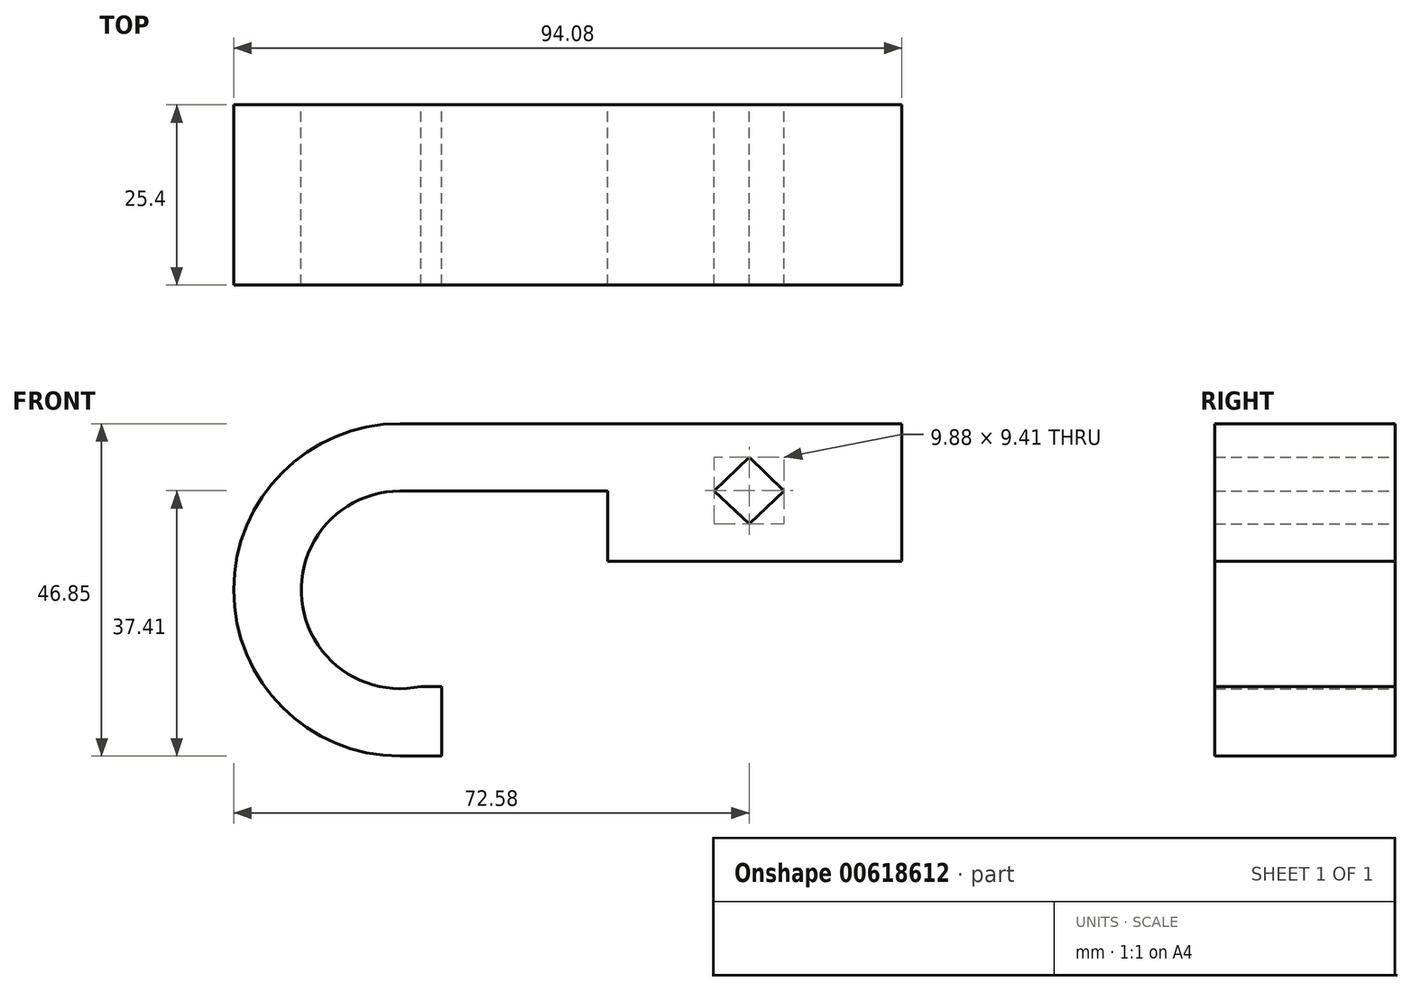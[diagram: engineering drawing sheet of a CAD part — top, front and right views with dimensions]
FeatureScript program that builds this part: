
annotation { "Feature Type Name" : "Feature", "Feature Type Description" : "" }
export const myFeature = defineFeature(function(context is Context, id is Id, definition is map)
    precondition{}
    {
        {
            var Q0;
            Q0=qCreatedBy(makeId("Front.planeOp"),FACE);
            var sketch = newSketch(context, id + "F0", { "sketchPlane" : qUnion([Q0])});
            skLineSegment(sketch, "E0.bottom", {"start": v(0, 0) * mm, "end": v(-70.66, 0) * mm});
            skLineSegment(sketch, "E0.left", {"start": v(0, 0) * mm, "end": v(0, -9.5) * mm});
            skPoint(sketch, "E1", {"position": v(-70.66, -23.42) * mm});
            skArc(sketch, "E2", {"start": v(-70.66, 0) * mm, "mid": v(-94.08, -23.42) * mm, "end": v(-70.66, -46.85) * mm});
            skArc(sketch, "E3", {"start": v(-70.66, -9.5) * mm, "mid": v(-84.5, -24.89) * mm, "end": v(-67.74, -37.03) * mm});
            skLineSegment(sketch, "E4", {"start": v(-67.74, -37.03) * mm, "end": v(-64.78, -37.03) * mm});
            skLineSegment(sketch, "E5", {"start": v(-64.78, -46.85) * mm, "end": v(-70.66, -46.85) * mm});
            skLineSegment(sketch, "E6", {"start": v(-64.78, -37.03) * mm, "end": v(-64.78, -46.85) * mm});
            skLineSegment(sketch, "E7.top", {"start": v(-41.44, -19.4) * mm, "end": v(0, -19.4) * mm});
            skLineSegment(sketch, "E7.left", {"start": v(-41.44, -9.5) * mm, "end": v(-41.44, -19.4) * mm});
            skLineSegment(sketch, "E7.right", {"start": v(0, -9.5) * mm, "end": v(0, -19.4) * mm});
            skLineSegment(sketch, "E8", {"start": v(-21.5, -4.73) * mm, "end": v(-16.56, -9.5) * mm});
            skLineSegment(sketch, "E9", {"start": v(-26.44, -9.5) * mm, "end": v(-21.5, -4.73) * mm});
            skLineSegment(sketch, "E10", {"start": v(-26.44, -9.5) * mm, "end": v(-21.5, -14.15) * mm});
            skLineSegment(sketch, "E11", {"start": v(-21.5, -14.15) * mm, "end": v(-16.56, -9.5) * mm});
            skLineSegment(sketch, "E12.trimOffspring", {"start": v(-41.44, -9.5) * mm, "end": v(-70.66, -9.5) * mm});
            skSolve(sketch);
        }
        {
            var Q0;
            Q0=makeQuery(id+"F0.imprint","IMPRINT",FACE,{"disambiguationData":[TD([[makeQuery(id+"F0.imprint","IMPRINT",EDGE,{"derivedFrom":sQuery(id+"F0.wireOp",EDGE,"E0.bottom")}),1.0]])]});
            extrude(context, id + "F1", {"entities" : qUnion([Q0]), "depth" : 25.4 * mm, "offsetDistance" : 25.4 * mm});
        }
    });
